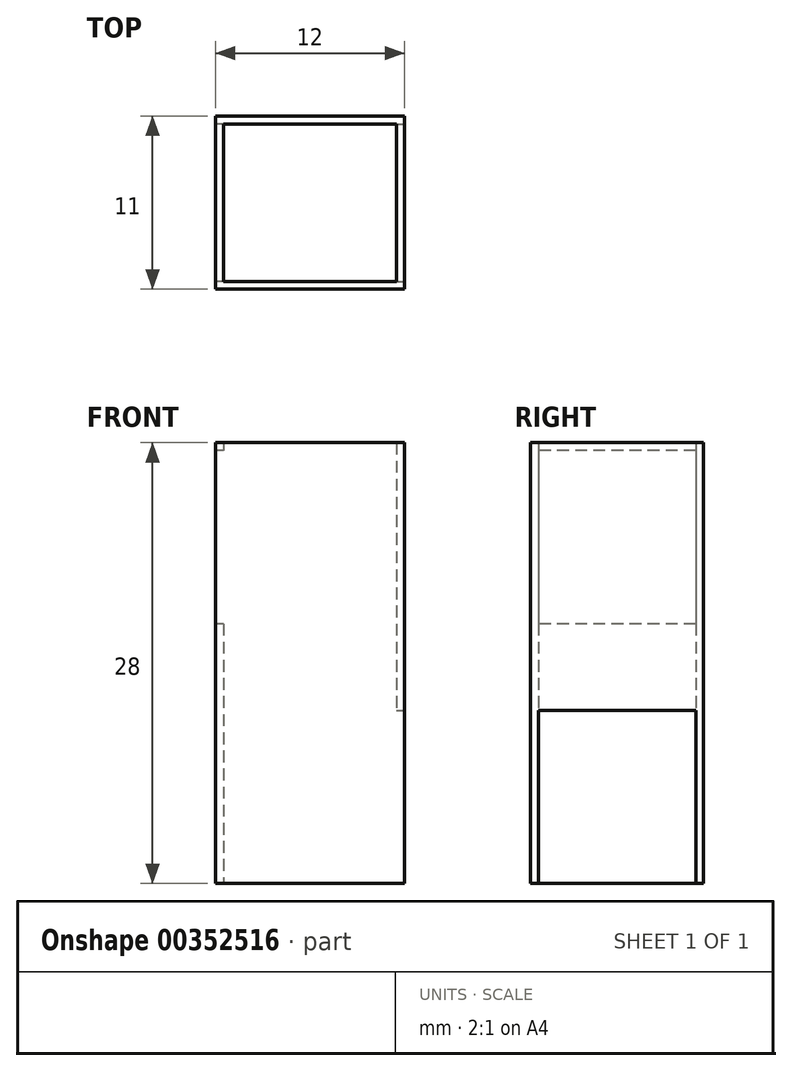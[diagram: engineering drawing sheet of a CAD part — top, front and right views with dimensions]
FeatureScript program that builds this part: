
annotation { "Feature Type Name" : "Feature", "Feature Type Description" : "" }
export const myFeature = defineFeature(function(context is Context, id is Id, definition is map)
    precondition{}
    {
        {
            var Q0;
            Q0=qCreatedBy(makeId("Top.planeOp"),FACE);
            var sketch = newSketch(context, id + "F0", { "sketchPlane" : qUnion([Q0])});
            skLineSegment(sketch, "E0.bottom", {"start": v(-7.68, 2.99) * mm, "end": v(4.32, 2.99) * mm});
            skLineSegment(sketch, "E0.top", {"start": v(-7.68, -8.01) * mm, "end": v(4.32, -8.01) * mm});
            skLineSegment(sketch, "E0.left", {"start": v(-7.68, 2.99) * mm, "end": v(-7.68, -8.01) * mm});
            skLineSegment(sketch, "E0.right", {"start": v(4.32, 2.99) * mm, "end": v(4.32, -8.01) * mm});
            skLineSegment(sketch, "E1.bottom", {"start": v(-7.18, 2.49) * mm, "end": v(3.82, 2.49) * mm});
            skLineSegment(sketch, "E1.top", {"start": v(-7.18, -7.51) * mm, "end": v(3.82, -7.51) * mm});
            skLineSegment(sketch, "E1.left", {"start": v(-7.18, 2.49) * mm, "end": v(-7.18, -7.51) * mm});
            skLineSegment(sketch, "E1.right", {"start": v(3.82, 2.49) * mm, "end": v(3.82, -7.51) * mm});
            skSolve(sketch);
        }
        {
            var Q0;
            Q0 = qSketchRegion(id + "F0", true);
            var Q1;
            Q1=sQuery(id+"F0.wireOp",EDGE,"E0.top");
            var Q2;
            Q2=sQuery(id+"F0.wireOp",EDGE,"E0.bottom");
            var Q3;
            Q3=sQuery(id+"F0.wireOp",EDGE,"E0.left");
            extrude(context, id + "F1", {"entities" : qUnion([Q0]), "surfaceEntities" : qUnion([Q1, Q2, Q3]), "depth" : 28 * mm});
        }
        {
            var Q0;
            Q0=makeQuery(id+"F1.opExtrude","SWEPT_FACE",FACE,{"disambiguationData":[OSD([sQuery(id+"F0.wireOp",EDGE,"E0.right")])]});
            var sketch = newSketch(context, id + "F2", { "sketchPlane" : qUnion([Q0])});
            skLineSegment(sketch, "E2.bottom", {"start": v(-7.51, 0) * mm, "end": v(2.49, 0) * mm});
            skLineSegment(sketch, "E2.top", {"start": v(-7.51, 11) * mm, "end": v(2.49, 11) * mm});
            skLineSegment(sketch, "E2.left", {"start": v(-7.51, 0) * mm, "end": v(-7.51, 11) * mm});
            skLineSegment(sketch, "E2.right", {"start": v(2.49, 0) * mm, "end": v(2.49, 11) * mm});
            skSolve(sketch);
        }
        {
            var Q0;
            Q0=makeQuery(id+"F2.imprint","IMPRINT",FACE,{"disambiguationData":[TD([[makeQuery(id+"F2.imprint","IMPRINT",EDGE,{"derivedFrom":sQuery(id+"F2.wireOp",EDGE,"E2.bottom")}),-1.0]])]});
            extrude(context, id + "F3", {"entities" : qUnion([Q0]), "operationType" : NewBodyOperationType.REMOVE, "oppositeDirection" : true, "depth" : 2 * mm});
        }
        {
            var Q0;
            Q0=makeQuery(id+"F1.opExtrude","SWEPT_FACE",FACE,{"disambiguationData":[OSD([sQuery(id+"F0.wireOp",EDGE,"E0.left")])]});
            var sketch = newSketch(context, id + "F4", { "sketchPlane" : qUnion([Q0])});
            skLineSegment(sketch, "E3.bottom", {"start": v(-2.49, 27.5) * mm, "end": v(7.51, 27.5) * mm});
            skLineSegment(sketch, "E3.top", {"start": v(-2.49, 16.5) * mm, "end": v(7.51, 16.5) * mm});
            skLineSegment(sketch, "E3.left", {"start": v(-2.49, 27.5) * mm, "end": v(-2.49, 16.5) * mm});
            skLineSegment(sketch, "E3.right", {"start": v(7.51, 27.5) * mm, "end": v(7.51, 16.5) * mm});
            skSolve(sketch);
        }
        {
            var Q0;
            Q0=makeQuery(id+"F4.imprint","IMPRINT",FACE,{"disambiguationData":[TD([[makeQuery(id+"F4.imprint","IMPRINT",EDGE,{"derivedFrom":sQuery(id+"F4.wireOp",EDGE,"E3.bottom")}),-1.0]])]});
            extrude(context, id + "F5", {"entities" : qUnion([Q0]), "operationType" : NewBodyOperationType.REMOVE, "oppositeDirection" : true, "depth" : 2 * mm});
        }
    });
